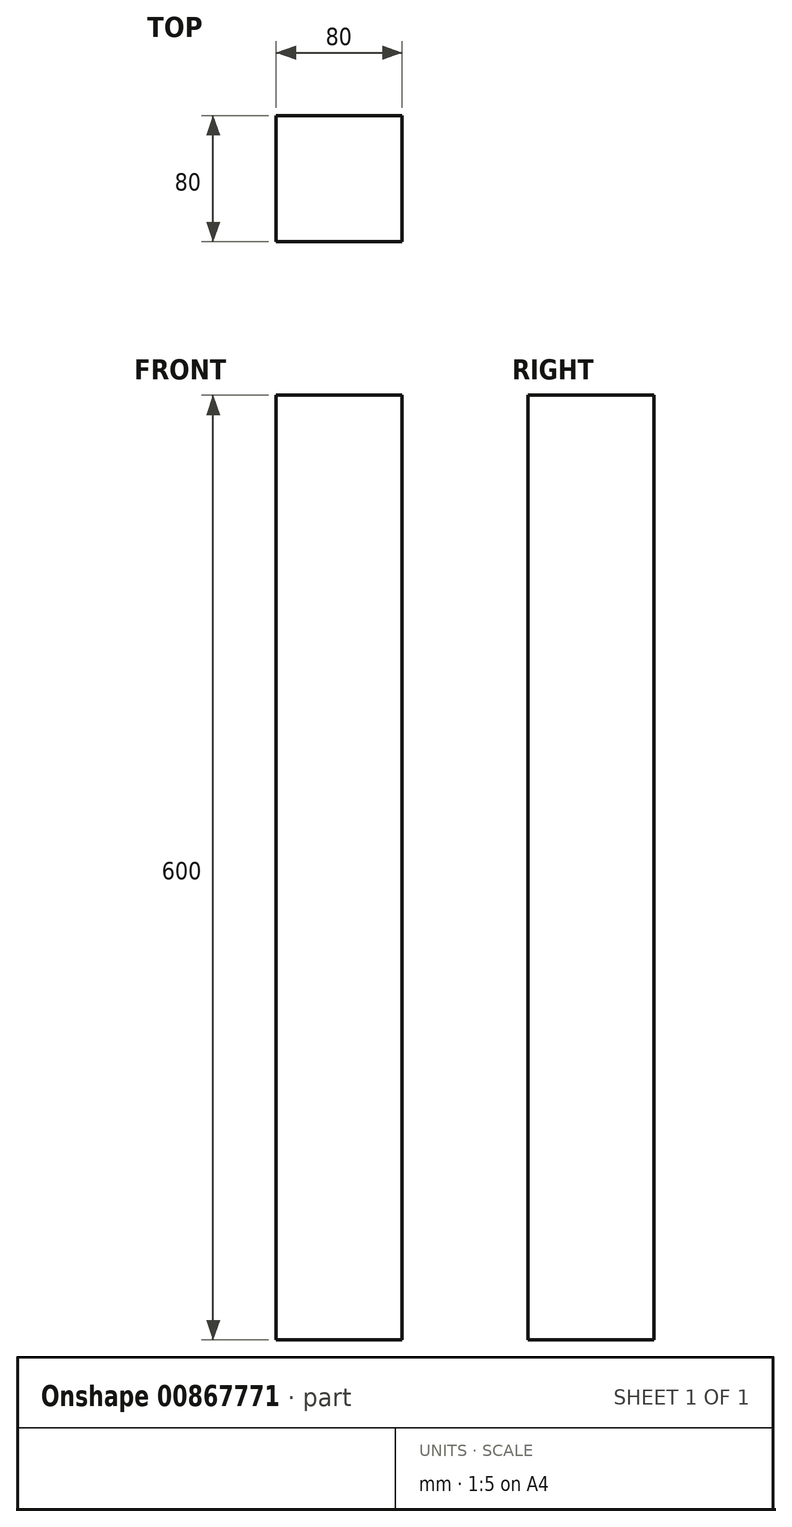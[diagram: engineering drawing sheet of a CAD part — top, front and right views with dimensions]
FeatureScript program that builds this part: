
annotation { "Feature Type Name" : "Feature", "Feature Type Description" : "" }
export const myFeature = defineFeature(function(context is Context, id is Id, definition is map)
    precondition{}
    {
        {
            var Q0;
            Q0=qCreatedBy(makeId("Top.planeOp"),FACE);
            var sketch = newSketch(context, id + "F0", { "sketchPlane" : qUnion([Q0])});
            skLineSegment(sketch, "E0.bottom", {"start": v(40, -40) * mm, "end": v(-40, -40) * mm});
            skLineSegment(sketch, "E0.top", {"start": v(40, 40) * mm, "end": v(-40, 40) * mm});
            skLineSegment(sketch, "E0.left", {"start": v(40, -40) * mm, "end": v(40, 40) * mm});
            skLineSegment(sketch, "E0.right", {"start": v(-40, -40) * mm, "end": v(-40, 40) * mm});
            skPoint(sketch, "E0.middle", {"position": v(0, 0) * mm});
            skSolve(sketch);
        }
        {
            var Q0;
            Q0=makeQuery(id+"F0.imprint","IMPRINT",FACE,{"disambiguationData":[TD([[makeQuery(id+"F0.imprint","IMPRINT",EDGE,{"derivedFrom":sQuery(id+"F0.wireOp",EDGE,"E0.bottom")}),-1.0]])]});
            extrude(context, id + "F1", {"entities" : qUnion([Q0]), "depth" : 600 * mm, "offsetDistance" : 25 * mm});
        }
    });
